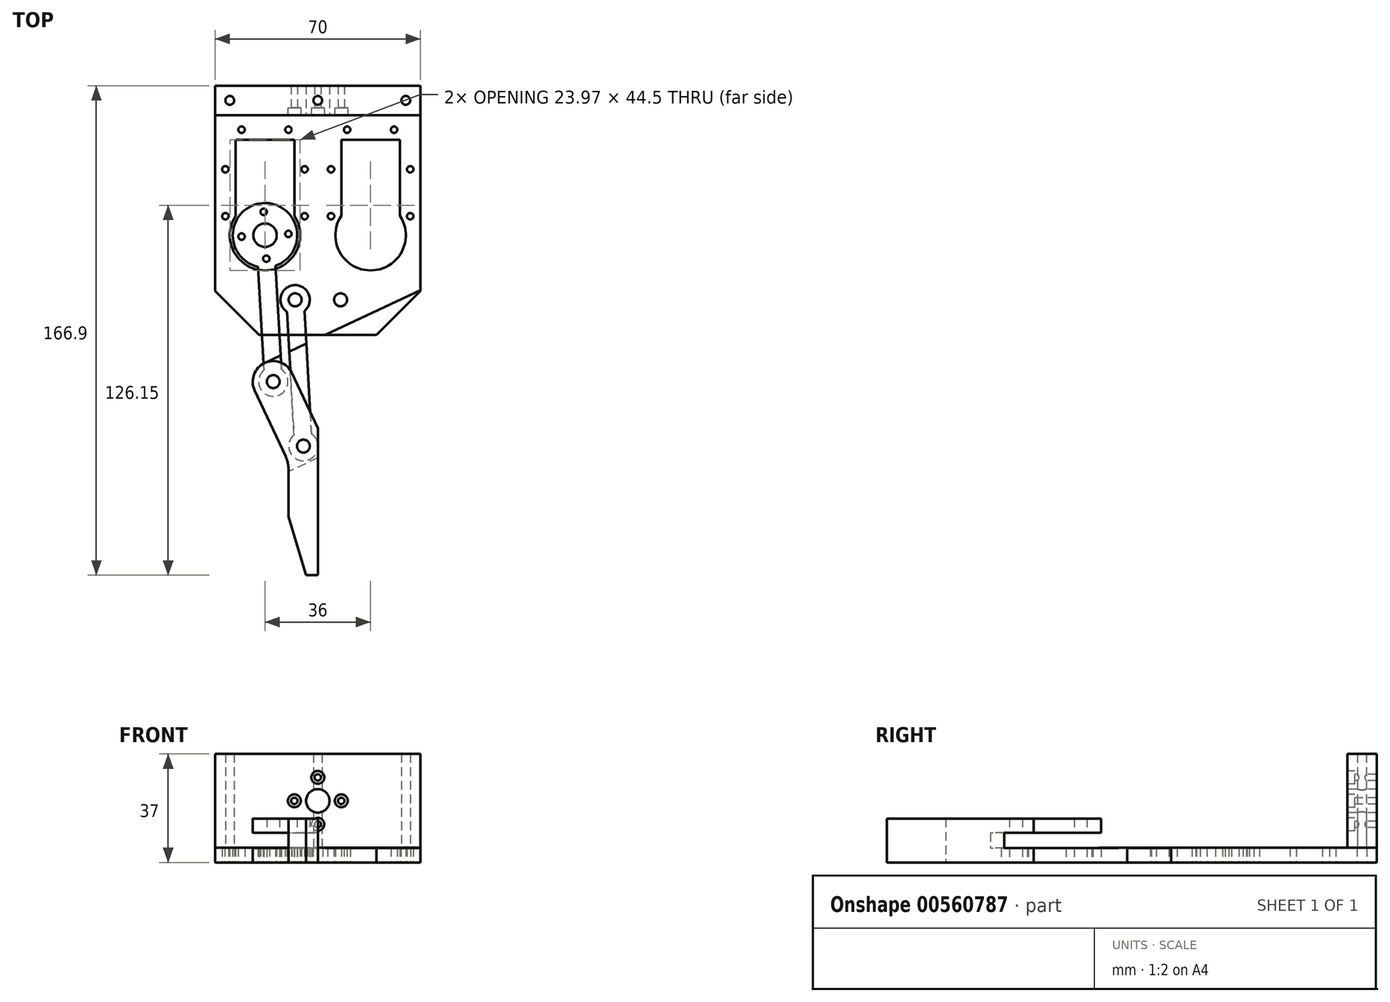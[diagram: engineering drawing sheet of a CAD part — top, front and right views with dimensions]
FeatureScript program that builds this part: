
annotation { "Feature Type Name" : "Feature", "Feature Type Description" : "" }
export const myFeature = defineFeature(function(context is Context, id is Id, definition is map)
    precondition{}
    {
        {
            var Q0;
            Q0=qCreatedBy(makeId("Top.planeOp"),FACE);
            var sketch = newSketch(context, id + "F0", { "sketchPlane" : qUnion([Q0])});
            skLineSegment(sketch, "E0.bottom", {"start": v(15, -15) * mm, "end": v(55, -15) * mm});
            skLineSegment(sketch, "E0.top", {"start": v(0, 70) * mm, "end": v(70, 70) * mm});
            skLineSegment(sketch, "E0.left", {"start": v(0, 0) * mm, "end": v(0, 70) * mm});
            skLineSegment(sketch, "E0.right", {"start": v(70, 0) * mm, "end": v(70, 70) * mm});
            skLineSegment(sketch, "E1.bottom", {"start": v(27, 51.5) * mm, "end": v(7, 51.5) * mm});
            skLineSegment(sketch, "E1.top", {"start": v(27, 25.63) * mm, "end": v(7, 25.63) * mm});
            skLineSegment(sketch, "E1.left", {"start": v(27, 51.5) * mm, "end": v(27, 25.63) * mm});
            skLineSegment(sketch, "E1.right", {"start": v(7, 51.5) * mm, "end": v(7, 25.63) * mm});
            skLineSegment(sketch, "E2", {"start": v(17, 51.5) * mm, "end": v(17, 19) * mm, "construction": true});
            skCircle(sketch, "E3", {"center": v(17, 19) * mm, "radius": 12 * mm});
            skPoint(sketch, "E4", {"position": v(30.5, 25.5) * mm});
            skPoint(sketch, "E5", {"position": v(30.5, 41.5) * mm});
            skPoint(sketch, "E6.MirrorP", {"position": v(3.5, 41.5) * mm});
            skPoint(sketch, "E7.MirrorP", {"position": v(3.5, 25.5) * mm});
            skPoint(sketch, "E8", {"position": v(25, 55) * mm});
            skPoint(sketch, "E9.MirrorP", {"position": v(9, 55) * mm});
            skPoint(sketch, "E10", {"position": v(30.5, 33.5) * mm});
            skPoint(sketch, "E11", {"position": v(30.5, 49.5) * mm});
            skPoint(sketch, "E12", {"position": v(3.5, 49.5) * mm});
            skPoint(sketch, "E13", {"position": v(3.5, 33.5) * mm});
            skLineSegment(sketch, "E14", {"start": v(0, 0) * mm, "end": v(15, -15) * mm});
            skLineSegment(sketch, "E15", {"start": v(55, -15) * mm, "end": v(70, 0) * mm});
            skPoint(sketch, "E16", {"position": v(27.26, -3) * mm});
            skLineSegment(sketch, "E17", {"start": v(35, 70) * mm, "end": v(35, 57.71) * mm, "construction": true});
            skPoint(sketch, "E18.MirrorP", {"position": v(53, 19) * mm});
            skPoint(sketch, "E19.MirrorP", {"position": v(42.74, -3) * mm});
            skPoint(sketch, "E20.MirrorP", {"position": v(66.5, 49.5) * mm});
            skPoint(sketch, "E21.MirrorP", {"position": v(66.5, 41.5) * mm});
            skPoint(sketch, "E22.MirrorP", {"position": v(66.5, 33.5) * mm});
            skPoint(sketch, "E23.MirrorP", {"position": v(66.5, 25.5) * mm});
            skPoint(sketch, "E24.MirrorP", {"position": v(39.5, 25.5) * mm});
            skPoint(sketch, "E25.MirrorP", {"position": v(39.5, 33.5) * mm});
            skPoint(sketch, "E26.MirrorP", {"position": v(39.5, 41.5) * mm});
            skPoint(sketch, "E27.MirrorP", {"position": v(39.5, 49.5) * mm});
            skPoint(sketch, "E28.MirrorP", {"position": v(45, 55) * mm});
            skPoint(sketch, "E29.MirrorP", {"position": v(61, 55) * mm});
            skLineSegment(sketch, "E30.MirrorCS", {"start": v(43, 51.5) * mm, "end": v(63, 51.5) * mm});
            skLineSegment(sketch, "E31.MirrorCS", {"start": v(43, 51.5) * mm, "end": v(43, 25.63) * mm});
            skLineSegment(sketch, "E32.MirrorCS", {"start": v(63, 51.5) * mm, "end": v(63, 25.63) * mm});
            skCircle(sketch, "E33.MirrorC", {"center": v(53, 19) * mm, "radius": 12 * mm});
            skLineSegment(sketch, "E34", {"start": v(27.26, -3) * mm, "end": v(17, 19) * mm, "construction": true});
            skPoint(sketch, "E35", {"position": v(5, 65) * mm});
            skPoint(sketch, "E36", {"position": v(65, 65) * mm});
            skPoint(sketch, "E37", {"position": v(35, 65) * mm});
            skSolve(sketch);
        }
        {
            var Q0;
            Q0=qSketchRegion(id+"F0",true);
            extrude(context, id + "F1", {"entities" : qUnion([Q0]), "depth" : 5 * mm});
        }
        {
            var Q0;
            Q0=sQuery(id+"F0.wireOp",VERTEX,"E9.MirrorP");
            var Q1;
            Q1=sQuery(id+"F0.wireOp",VERTEX,"E6.MirrorP");
            var Q2;
            Q2=sQuery(id+"F0.wireOp",VERTEX,"E7.MirrorP");
            var Q3;
            Q3=sQuery(id+"F0.wireOp",VERTEX,"E4");
            var Q4;
            Q4=sQuery(id+"F0.wireOp",VERTEX,"E5");
            var Q5;
            Q5=sQuery(id+"F0.wireOp",VERTEX,"E24.MirrorP");
            var Q6;
            Q6=sQuery(id+"F0.wireOp",VERTEX,"E26.MirrorP");
            var Q7;
            Q7=sQuery(id+"F0.wireOp",VERTEX,"E21.MirrorP");
            var Q8;
            Q8=sQuery(id+"F0.wireOp",VERTEX,"E23.MirrorP");
            var Q9;
            Q9=sQuery(id+"F0.wireOp",VERTEX,"E29.MirrorP");
            var Q10;
            Q10=sQuery(id+"F0.wireOp",VERTEX,"E28.MirrorP");
            var Q11;
            Q11=sQuery(id+"F0.wireOp",VERTEX,"E8");
            var Q12;
            Q12=makeQuery(id+"F1.opExtrude","SWEPT_BODY",BODY,{"disambiguationData":[OSD([sQuery(id+"F0.wireOp",EDGE,"E0.bottom"),sQuery(id+"F0.wireOp",EDGE,"E0.top"),sQuery(id+"F0.wireOp",EDGE,"E0.left"),sQuery(id+"F0.wireOp",EDGE,"E0.right"),sQuery(id+"F0.wireOp",EDGE,"E1.bottom"),sQuery(id+"F0.wireOp",EDGE,"E1.left"),sQuery(id+"F0.wireOp",EDGE,"E1.right"),sQuery(id+"F0.wireOp",EDGE,"E14"),sQuery(id+"F0.wireOp",EDGE,"E15"),sQuery(id+"F0.wireOp",EDGE,"E30.MirrorCS"),sQuery(id+"F0.wireOp",EDGE,"E31.MirrorCS"),sQuery(id+"F0.wireOp",EDGE,"E32.MirrorCS"),sQuery(id+"F0.wireOp",EDGE,"E33.MirrorC"),sQuery(id+"F0.wireOp",EDGE,"E3")])]});
            hole(context, id + "F2", {"style" : HoleStyle.SIMPLE, "endStyle" : HoleEndStyle.THROUGH, "oppositeDirection" : true, "holeDiameter" : 2.2 * mm, "isTappedThrough" : true, "tappedDepth" : 6.2 * mm, "tapClearance" : 3, "locations" : qUnion([Q0, Q1, Q2, Q3, Q4, Q5, Q6, Q7, Q8, Q9, Q10, Q11]), "scope" : qUnion([Q12])});
        }
        {
            var Q0;
            Q0=sQuery(id+"F0.wireOp",VERTEX,"E16");
            var Q1;
            Q1=sQuery(id+"F0.wireOp",VERTEX,"E19.MirrorP");
            var Q2;
            Q2=makeQuery(id+"F1.opExtrude","SWEPT_BODY",BODY,{"disambiguationData":[OSD([sQuery(id+"F0.wireOp",EDGE,"E0.bottom"),sQuery(id+"F0.wireOp",EDGE,"E0.top"),sQuery(id+"F0.wireOp",EDGE,"E0.left"),sQuery(id+"F0.wireOp",EDGE,"E0.right"),sQuery(id+"F0.wireOp",EDGE,"E1.bottom"),sQuery(id+"F0.wireOp",EDGE,"E1.left"),sQuery(id+"F0.wireOp",EDGE,"E1.right"),sQuery(id+"F0.wireOp",EDGE,"E14"),sQuery(id+"F0.wireOp",EDGE,"E15"),sQuery(id+"F0.wireOp",EDGE,"E30.MirrorCS"),sQuery(id+"F0.wireOp",EDGE,"E31.MirrorCS"),sQuery(id+"F0.wireOp",EDGE,"E32.MirrorCS"),sQuery(id+"F0.wireOp",EDGE,"E33.MirrorC"),sQuery(id+"F0.wireOp",EDGE,"E3")])]});
            hole(context, id + "F3", {"style" : HoleStyle.SIMPLE, "endStyle" : HoleEndStyle.THROUGH, "oppositeDirection" : true, "standardTappedOrClearance" : lookupTablePath({ "standard" : "ISO", "fit" : "Normal", "size" : "M4", "type" : "Clearance" }), "standardBlindInLast" : lookupTablePath({ "fit" : "Standard", "standard" : "ISO", "size" : "M4", "type" : "Clearance" }), "holeDiameter" : 4.4 * mm, "isTappedThrough" : true, "tappedDepth" : 6.2 * mm, "tapClearance" : 3, "locations" : qUnion([Q0, Q1]), "scope" : qUnion([Q2])});
        }
        {
            var Q0;
            Q0=sQuery(id+"F0.wireOp",VERTEX,"E35");
            var Q1;
            Q1=sQuery(id+"F0.wireOp",VERTEX,"E37");
            var Q2;
            Q2=sQuery(id+"F0.wireOp",VERTEX,"E36");
            var Q3;
            Q3=makeQuery(id+"F1.opExtrude","SWEPT_BODY",BODY,{"disambiguationData":[OSD([sQuery(id+"F0.wireOp",EDGE,"E0.bottom"),sQuery(id+"F0.wireOp",EDGE,"E0.top"),sQuery(id+"F0.wireOp",EDGE,"E0.left"),sQuery(id+"F0.wireOp",EDGE,"E0.right"),sQuery(id+"F0.wireOp",EDGE,"E1.bottom"),sQuery(id+"F0.wireOp",EDGE,"E1.left"),sQuery(id+"F0.wireOp",EDGE,"E1.right"),sQuery(id+"F0.wireOp",EDGE,"E14"),sQuery(id+"F0.wireOp",EDGE,"E15"),sQuery(id+"F0.wireOp",EDGE,"E30.MirrorCS"),sQuery(id+"F0.wireOp",EDGE,"E31.MirrorCS"),sQuery(id+"F0.wireOp",EDGE,"E32.MirrorCS"),sQuery(id+"F0.wireOp",EDGE,"E33.MirrorC"),sQuery(id+"F0.wireOp",EDGE,"E3")])]});
            hole(context, id + "F4", {"style" : HoleStyle.SIMPLE, "endStyle" : HoleEndStyle.THROUGH, "oppositeDirection" : true, "standardTappedOrClearance" : lookupTablePath({ "standard" : "ISO", "fit" : "Normal", "size" : "M3", "type" : "Clearance" }), "standardBlindInLast" : lookupTablePath({ "fit" : "Standard", "standard" : "ISO", "size" : "M3", "type" : "Clearance" }), "holeDiameter" : 3.3 * mm, "isTappedThrough" : true, "tappedDepth" : 6.2 * mm, "tapClearance" : 3, "locations" : qUnion([Q0, Q1, Q2]), "scope" : qUnion([Q3])});
        }
        {
            var Q0;
            Q0=makeQuery(id+"F1.opExtrude","CAP_FACE",FACE,{"disambiguationData":[OSD([sQuery(id+"F0.wireOp",EDGE,"E0.bottom"),sQuery(id+"F0.wireOp",EDGE,"E0.top"),sQuery(id+"F0.wireOp",EDGE,"E0.left"),sQuery(id+"F0.wireOp",EDGE,"E0.right"),sQuery(id+"F0.wireOp",EDGE,"E1.bottom"),sQuery(id+"F0.wireOp",EDGE,"E1.left"),sQuery(id+"F0.wireOp",EDGE,"E1.right"),sQuery(id+"F0.wireOp",EDGE,"E14"),sQuery(id+"F0.wireOp",EDGE,"E15"),sQuery(id+"F0.wireOp",EDGE,"E30.MirrorCS"),sQuery(id+"F0.wireOp",EDGE,"E31.MirrorCS"),sQuery(id+"F0.wireOp",EDGE,"E32.MirrorCS"),sQuery(id+"F0.wireOp",EDGE,"E33.MirrorC"),sQuery(id+"F0.wireOp",EDGE,"E3")])],"isStart":false});
            var sketch = newSketch(context, id + "F5", { "sketchPlane" : qUnion([Q0])});
            skLineSegment(sketch, "E38.bottom", {"start": v(0, 70) * mm, "end": v(70, 70) * mm});
            skLineSegment(sketch, "E38.top", {"start": v(0, 60) * mm, "end": v(70, 60) * mm});
            skLineSegment(sketch, "E38.left", {"start": v(0, 70) * mm, "end": v(0, 60) * mm});
            skLineSegment(sketch, "E38.right", {"start": v(70, 70) * mm, "end": v(70, 60) * mm});
            skCircle(sketch, "E39", {"center": v(5, 65) * mm, "radius": 1.5 * mm});
            skCircle(sketch, "E40", {"center": v(35, 65) * mm, "radius": 1.5 * mm});
            skCircle(sketch, "E41", {"center": v(65, 65) * mm, "radius": 1.5 * mm});
            skSolve(sketch);
        }
        {
            var Q0;
            Q0=makeQuery(id+"F5.imprint","IMPRINT",FACE,{"disambiguationData":[TD([[makeQuery(id+"F5.imprint","IMPRINT",EDGE,{"derivedFrom":sQuery(id+"F5.wireOp",EDGE,"E39")}),-1.0]])]});
            var Q1;
            Q1=makeQuery(id+"F5.imprint","IMPRINT",FACE,{"disambiguationData":[TD([[makeQuery(id+"F5.imprint","IMPRINT",EDGE,{"derivedFrom":sQuery(id+"F5.wireOp",EDGE,"E40")}),-1.0]])]});
            var Q2;
            Q2=makeQuery(id+"F5.imprint","IMPRINT",FACE,{"disambiguationData":[TD([[makeQuery(id+"F5.imprint","IMPRINT",EDGE,{"derivedFrom":sQuery(id+"F5.wireOp",EDGE,"E38.bottom")}),-1.0]])]});
            var Q3;
            Q3=makeQuery(id+"F5.imprint","IMPRINT",FACE,{"disambiguationData":[TD([[makeQuery(id+"F5.imprint","IMPRINT",EDGE,{"derivedFrom":sQuery(id+"F5.wireOp",EDGE,"E41")}),-1.0]])]});
            extrude(context, id + "F6", {"entities" : qUnion([Q0, Q1, Q2, Q3]), "depth" : 32 * mm});
        }
        {
            var Q0;
            Q0=makeQuery(id+"F6.opExtrude","SWEPT_FACE",FACE,{"disambiguationData":[OSD([sQuery(id+"F5.wireOp",EDGE,"E38.top")])]});
            var sketch = newSketch(context, id + "F7", { "sketchPlane" : qUnion([Q0])});
            skCircle(sketch, "E42", {"center": v(35, 21) * mm, "radius": 8 * mm, "construction": true});
            skCircle(sketch, "E43", {"center": v(35, 29) * mm, "radius": 1.1 * mm});
            skCircle(sketch, "E44.1.0", {"center": v(27, 21) * mm, "radius": 1.1 * mm});
            skCircle(sketch, "E44.2.0", {"center": v(35, 13) * mm, "radius": 1.1 * mm});
            skCircle(sketch, "E44.3.0", {"center": v(43, 21) * mm, "radius": 1.1 * mm});
            skCircle(sketch, "E45", {"center": v(35, 21) * mm, "radius": 4 * mm});
            skSolve(sketch);
        }
        {
            var Q0;
            Q0=qSketchRegion(id+"F7",true);
            extrude(context, id + "F8", {"entities" : qUnion([Q0]), "operationType" : NewBodyOperationType.REMOVE, "endBound" : BoundingType.THROUGH_ALL, "oppositeDirection" : true, "depth" : 25 * mm});
        }
        {
            var Q0;
            Q0=qCreatedBy(makeId("Top.planeOp"),FACE);
            var sketch = newSketch(context, id + "F9", { "sketchPlane" : qUnion([Q0])});
            skLineSegment(sketch, "E46", {"start": v(14, 18.83) * mm, "end": v(16.83, -31.09) * mm});
            skLineSegment(sketch, "E47", {"start": v(16.83, -31.09) * mm, "end": v(22.82, -30.75) * mm});
            skLineSegment(sketch, "E48", {"start": v(22.82, -30.75) * mm, "end": v(20, 19.17) * mm});
            skLineSegment(sketch, "E49", {"start": v(20, 19.17) * mm, "end": v(14, 18.83) * mm});
            skCircle(sketch, "E50", {"center": v(27.26, -3) * mm, "radius": 5 * mm});
            skCircle(sketch, "E51", {"center": v(19.82, -30.92) * mm, "radius": 5 * mm});
            skCircle(sketch, "E52", {"center": v(17, 19) * mm, "radius": 8 * mm, "construction": true});
            skLineSegment(sketch, "E53", {"start": v(24.26, -3.17) * mm, "end": v(30.25, -2.83) * mm});
            skLineSegment(sketch, "E54", {"start": v(24.26, -3.17) * mm, "end": v(27.09, -53.09) * mm});
            skLineSegment(sketch, "E55", {"start": v(27.09, -53.09) * mm, "end": v(33.08, -52.75) * mm});
            skLineSegment(sketch, "E56", {"start": v(33.08, -52.75) * mm, "end": v(30.25, -2.83) * mm});
            skCircle(sketch, "E57", {"center": v(30.08, -52.92) * mm, "radius": 5 * mm});
            skCircle(sketch, "E58.0", {"center": v(27.26, -3) * mm, "radius": 2.2 * mm});
            skCircle(sketch, "E59", {"center": v(30.08, -52.92) * mm, "radius": 2.2 * mm});
            skCircle(sketch, "E60", {"center": v(19.82, -30.92) * mm, "radius": 2.2 * mm});
            skLineSegment(sketch, "E61", {"start": v(30.08, -52.92) * mm, "end": v(19.82, -30.92) * mm, "construction": true});
            skCircle(sketch, "E62", {"center": v(17, 19) * mm, "radius": 11 * mm});
            skLineSegment(sketch, "E63", {"start": v(16.55, 26.99) * mm, "end": v(17.8, 4.71) * mm, "construction": true});
            skCircle(sketch, "E64", {"center": v(17, 19) * mm, "radius": 4 * mm});
            skCircle(sketch, "E65", {"center": v(16.55, 26.99) * mm, "radius": 1.1 * mm});
            skCircle(sketch, "E66.1.0", {"center": v(9.01, 18.55) * mm, "radius": 1.1 * mm});
            skCircle(sketch, "E66.2.0", {"center": v(17.45, 11.01) * mm, "radius": 1.1 * mm});
            skCircle(sketch, "E66.3.0", {"center": v(24.99, 19.45) * mm, "radius": 1.1 * mm});
            skSolve(sketch);
        }
        {
            var Q0;
            Q0=makeQuery(id+"F9.imprint","IMPRINT",FACE,{"disambiguationData":[TD([[makeQuery(id+"F9.imprint","IMPRINT",EDGE,{"derivedFrom":sQuery(id+"F9.wireOp",EDGE,"648b47fd-c98e-4e7c-a0a6-51eef2966ebb.1.0")}),-1.0]])]});
            var Q1;
            {var subQ1=sQuery(id+"F9.wireOp",EDGE,"E47");var subQ7=sQuery(id+"F9.wireOp",EDGE,"E46");var subQ8=makeQuery(id+"F9.imprint","INTERSECT",VERTEX,{"derivedFrom":[subQ7,subQ1]});Q1=makeQuery(id+"F9.imprint","IMPRINT",FACE,{"disambiguationData":[TD([[makeQuery(id+"F9.imprint","IMPRINT",EDGE,{"disambiguationData":[TD([[subQ8,1.0]])],"derivedFrom":subQ7}),-1.0]])]});}
            var Q2;
            {var subQ1=sQuery(id+"F9.wireOp",EDGE,"E47");var subQ7=sQuery(id+"F9.wireOp",EDGE,"E46");var subQ8=makeQuery(id+"F9.imprint","INTERSECT",VERTEX,{"derivedFrom":[subQ7,subQ1]});Q2=makeQuery(id+"F9.imprint","IMPRINT",FACE,{"disambiguationData":[TD([[makeQuery(id+"F9.imprint","IMPRINT",EDGE,{"disambiguationData":[TD([[subQ8,1.0]])],"derivedFrom":subQ7}),1.0]])]});}
            var Q3;
            {var subQ0=sQuery(id+"F9.wireOp",EDGE,"E54");var subQ1=sQuery(id+"F9.wireOp",EDGE,"E50");var subQ2=makeQuery(id+"F9.imprint","INTERSECT",VERTEX,{"derivedFrom":[subQ1,subQ0]});Q3=makeQuery(id+"F9.imprint","IMPRINT",FACE,{"disambiguationData":[TD([[makeQuery(id+"F9.imprint","IMPRINT",EDGE,{"disambiguationData":[TD([[subQ2,-1.0]])],"derivedFrom":subQ1}),-1.0]])]});}
            var Q4;
            {var subQ0=sQuery(id+"F9.wireOp",EDGE,"E54");var subQ3=sQuery(id+"F9.wireOp",EDGE,"E50");var subQ4=makeQuery(id+"F9.imprint","INTERSECT",VERTEX,{"derivedFrom":[subQ3,subQ0]});Q4=makeQuery(id+"F9.imprint","IMPRINT",FACE,{"disambiguationData":[TD([[makeQuery(id+"F9.imprint","IMPRINT",EDGE,{"disambiguationData":[TD([[subQ4,1.0]])],"derivedFrom":subQ3}),1.0]])]});}
            var Q5;
            {var subQ0=sQuery(id+"F9.wireOp",EDGE,"E54");var subQ3=sQuery(id+"F9.wireOp",EDGE,"E50");var subQ4=makeQuery(id+"F9.imprint","INTERSECT",VERTEX,{"derivedFrom":[subQ3,subQ0]});Q5=makeQuery(id+"F9.imprint","IMPRINT",FACE,{"disambiguationData":[TD([[makeQuery(id+"F9.imprint","IMPRINT",EDGE,{"disambiguationData":[TD([[subQ4,-1.0]])],"derivedFrom":subQ3}),1.0]])]});}
            var Q6;
            {var subQ1=sQuery(id+"F9.wireOp",EDGE,"E55");var subQ7=sQuery(id+"F9.wireOp",EDGE,"E54");var subQ8=makeQuery(id+"F9.imprint","INTERSECT",VERTEX,{"derivedFrom":[subQ7,subQ1]});Q6=makeQuery(id+"F9.imprint","IMPRINT",FACE,{"disambiguationData":[TD([[makeQuery(id+"F9.imprint","IMPRINT",EDGE,{"disambiguationData":[TD([[subQ8,1.0]])],"derivedFrom":subQ7}),1.0]])]});}
            var Q7;
            {var subQ1=sQuery(id+"F9.wireOp",EDGE,"E55");var subQ7=sQuery(id+"F9.wireOp",EDGE,"E54");var subQ8=makeQuery(id+"F9.imprint","INTERSECT",VERTEX,{"derivedFrom":[subQ7,subQ1]});Q7=makeQuery(id+"F9.imprint","IMPRINT",FACE,{"disambiguationData":[TD([[makeQuery(id+"F9.imprint","IMPRINT",EDGE,{"disambiguationData":[TD([[subQ8,1.0]])],"derivedFrom":subQ7}),-1.0]])]});}
            var Q8;
            {var subQ0=sQuery(id+"F9.wireOp",EDGE,"E62");var subQ1=sQuery(id+"F9.wireOp",EDGE,"E46");var subQ2=makeQuery(id+"F9.imprint","INTERSECT",VERTEX,{"derivedFrom":[subQ1,subQ0]});Q8=makeQuery(id+"F9.imprint","IMPRINT",FACE,{"disambiguationData":[TD([[makeQuery(id+"F9.imprint","IMPRINT",EDGE,{"disambiguationData":[TD([[subQ2,-1.0]])],"derivedFrom":subQ1}),1.0]])]});}
            var Q9;
            Q9=makeQuery(id+"F9.imprint","IMPRINT",FACE,{"disambiguationData":[TD([[makeQuery(id+"F9.imprint","IMPRINT",EDGE,{"derivedFrom":sQuery(id+"F9.wireOp",EDGE,"E65")}),-1.0]])]});
            var Q10;
            Q10=makeQuery(id+"F9.imprint","IMPRINT",FACE,{"disambiguationData":[TD([[makeQuery(id+"F9.imprint","IMPRINT",EDGE,{"derivedFrom":sQuery(id+"F9.wireOp",EDGE,"E66.2.0")}),-1.0]])]});
            extrude(context, id + "F10", {"entities" : qUnion([Q0, Q1, Q2, Q3, Q4, Q5, Q6, Q7, Q8, Q9, Q10]), "depth" : 5 * mm});
        }
        {
            var Q0;
            Q0=qCreatedBy(makeId("Top.planeOp"),FACE);
            var sketch = newSketch(context, id + "F11", { "sketchPlane" : qUnion([Q0])});
            skLineSegment(sketch, "E67", {"start": v(35, -46.9) * mm, "end": v(23.2, -21.62) * mm});
            skLineSegment(sketch, "E68", {"start": v(10.52, -27.53) * mm, "end": v(25, -58.58) * mm});
            skLineSegment(sketch, "E69", {"start": v(23.2, -21.62) * mm, "end": v(10.52, -27.53) * mm});
            skLineSegment(sketch, "E70", {"start": v(35, -46.9) * mm, "end": v(35, -96.9) * mm});
            skLineSegment(sketch, "E71", {"start": v(35, -96.9) * mm, "end": v(31, -96.9) * mm});
            skLineSegment(sketch, "E72", {"start": v(25, -58.58) * mm, "end": v(25, -76.9) * mm});
            skLineSegment(sketch, "E73", {"start": v(25, -76.9) * mm, "end": v(31, -96.9) * mm});
            skCircle(sketch, "E74.0", {"center": v(30.08, -52.92) * mm, "radius": 2.2 * mm});
            skCircle(sketch, "E74.1", {"center": v(19.82, -30.92) * mm, "radius": 2.2 * mm});
            skSolve(sketch);
        }
        {
            var Q0;
            Q0=qSketchRegion(id+"F11",true);
            extrude(context, id + "F12", {"entities" : qUnion([Q0]), "depth" : 15 * mm});
        }
        {
            var Q0;
            Q0=makeQuery(id+"F12.opExtrude","SWEPT_FACE",FACE,{"disambiguationData":[OSD([sQuery(id+"F11.wireOp",EDGE,"E68")])]});
            var sketch = newSketch(context, id + "F13", { "sketchPlane" : qUnion([Q0])});
            skLineSegment(sketch, "E75.bottom", {"start": v(29.4, 4.9) * mm, "end": v(66.4, 4.9) * mm});
            skLineSegment(sketch, "E75.top", {"start": v(29.4, 10.1) * mm, "end": v(66.4, 10.1) * mm});
            skLineSegment(sketch, "E75.left", {"start": v(29.4, 4.9) * mm, "end": v(29.4, 10.1) * mm});
            skLineSegment(sketch, "E75.right", {"start": v(66.4, 4.9) * mm, "end": v(66.4, 10.1) * mm});
            skSolve(sketch);
        }
        {
            var Q0;
            Q0=qSketchRegion(id+"F13",true);
            extrude(context, id + "F14", {"entities" : qUnion([Q0]), "operationType" : NewBodyOperationType.REMOVE, "endBound" : BoundingType.THROUGH_ALL, "oppositeDirection" : true, "depth" : 25 * mm, "hasSecondDirection" : true, "secondDirectionBound" : SecondDirectionBoundingType.THROUGH_ALL, "secondDirectionOppositeDirection" : false, "secondDirectionDepth" : 25 * mm});
        }
        {
            var Q0;
            {var subQ0=sQuery(id+"F11.wireOp",EDGE,"E69");var subQ1=sQuery(id+"F11.wireOp",EDGE,"E68");Q0=makeQuery(id+"F14.boolean.opBoolean","SPLIT",EDGE,{"disambiguationData":[TD([makeQuery(id+"F14.opExtrude","SWEPT_FACE",FACE,{"disambiguationData":[OSD([sQuery(id+"F13.wireOp",EDGE,"E75.top")])]})])],"derivedFrom":makeQuery(id+"F12.opExtrude","SWEPT_EDGE",EDGE,{"disambiguationData":[OSD([subQ1,subQ0])]})});}
            var Q1;
            {var subQ0=sQuery(id+"F11.wireOp",EDGE,"E69");var subQ1=sQuery(id+"F11.wireOp",EDGE,"E68");Q1=makeQuery(id+"F14.boolean.opBoolean","SPLIT",EDGE,{"disambiguationData":[TD([makeQuery(id+"F14.opExtrude","SWEPT_FACE",FACE,{"disambiguationData":[OSD([sQuery(id+"F13.wireOp",EDGE,"E75.bottom")])]})])],"derivedFrom":makeQuery(id+"F12.opExtrude","SWEPT_EDGE",EDGE,{"disambiguationData":[OSD([subQ1,subQ0])]})});}
            var Q2;
            {var subQ0=sQuery(id+"F11.wireOp",EDGE,"E67");var subQ1=sQuery(id+"F11.wireOp",EDGE,"E69");Q2=makeQuery(id+"F14.boolean.opBoolean","SPLIT",EDGE,{"disambiguationData":[TD([makeQuery(id+"F14.opExtrude","SWEPT_FACE",FACE,{"disambiguationData":[OSD([sQuery(id+"F13.wireOp",EDGE,"E75.top")])]})])],"derivedFrom":makeQuery(id+"F12.opExtrude","SWEPT_EDGE",EDGE,{"disambiguationData":[OSD([subQ0,subQ1])]})});}
            var Q3;
            {var subQ0=sQuery(id+"F11.wireOp",EDGE,"E67");var subQ1=sQuery(id+"F11.wireOp",EDGE,"E69");Q3=makeQuery(id+"F14.boolean.opBoolean","SPLIT",EDGE,{"disambiguationData":[TD([makeQuery(id+"F14.opExtrude","SWEPT_FACE",FACE,{"disambiguationData":[OSD([sQuery(id+"F13.wireOp",EDGE,"E75.bottom")])]})])],"derivedFrom":makeQuery(id+"F12.opExtrude","SWEPT_EDGE",EDGE,{"disambiguationData":[OSD([subQ0,subQ1])]})});}
            fillet(context, id + "F15", {"entities" : qUnion([Q0, Q1, Q2, Q3]), "radius" : 7 * mm, "tangentPropagation" : true, "allowEdgeOverflow" : false});
        }
        {
            var Q0;
            {var subQ0=sQuery(id+"F11.wireOp",EDGE,"E72");var subQ1=sQuery(id+"F11.wireOp",EDGE,"E68");Q0=makeQuery(id+"F14.boolean.opBoolean","SPLIT",EDGE,{"disambiguationData":[TD([makeQuery(id+"F14.opExtrude","SWEPT_FACE",FACE,{"disambiguationData":[OSD([sQuery(id+"F13.wireOp",EDGE,"E75.top")])]})])],"derivedFrom":makeQuery(id+"F12.opExtrude","SWEPT_EDGE",EDGE,{"disambiguationData":[OSD([subQ1,subQ0])]})});}
            var Q1;
            {var subQ0=sQuery(id+"F11.wireOp",EDGE,"E72");var subQ1=sQuery(id+"F11.wireOp",EDGE,"E68");Q1=makeQuery(id+"F14.boolean.opBoolean","SPLIT",EDGE,{"disambiguationData":[TD([makeQuery(id+"F14.opExtrude","SWEPT_FACE",FACE,{"disambiguationData":[OSD([sQuery(id+"F13.wireOp",EDGE,"E75.bottom")])]})])],"derivedFrom":makeQuery(id+"F12.opExtrude","SWEPT_EDGE",EDGE,{"disambiguationData":[OSD([subQ1,subQ0])]})});}
            fillet(context, id + "F16", {"entities" : qUnion([Q0, Q1]), "radius" : 10 * mm, "tangentPropagation" : true, "allowEdgeOverflow" : false});
        }
        {
            var Q0;
            Q0=sQuery(id+"F7.wireOp",VERTEX,"E43.center");
            var Q1;
            Q1=sQuery(id+"F7.wireOp",VERTEX,"E44.3.0.center");
            var Q2;
            Q2=sQuery(id+"F7.wireOp",VERTEX,"E44.2.0.center");
            var Q3;
            Q3=sQuery(id+"F7.wireOp",VERTEX,"E44.1.0.center");
            var Q4;
            Q4=makeQuery(id+"F6.opExtrude","SWEPT_BODY",BODY,{"disambiguationData":[OSD([sQuery(id+"F5.wireOp",EDGE,"E38.bottom"),sQuery(id+"F5.wireOp",EDGE,"E38.top"),sQuery(id+"F5.wireOp",EDGE,"E38.left"),sQuery(id+"F5.wireOp",EDGE,"E38.right"),sQuery(id+"F5.wireOp",EDGE,"E39"),sQuery(id+"F5.wireOp",EDGE,"E40"),sQuery(id+"F5.wireOp",EDGE,"E41")])]});
            hole(context, id + "F17", {"style" : HoleStyle.C_BORE, "endStyle" : HoleEndStyle.THROUGH, "holeDiameter" : 2.2 * mm, "cBoreDiameter" : 4.4 * mm, "cBoreDepth" : 2.5 * mm, "isTappedThrough" : true, "tappedDepth" : 6.2 * mm, "tapClearance" : 3, "locations" : qUnion([Q0, Q1, Q2, Q3]), "scope" : qUnion([Q4])});
        }
    });
